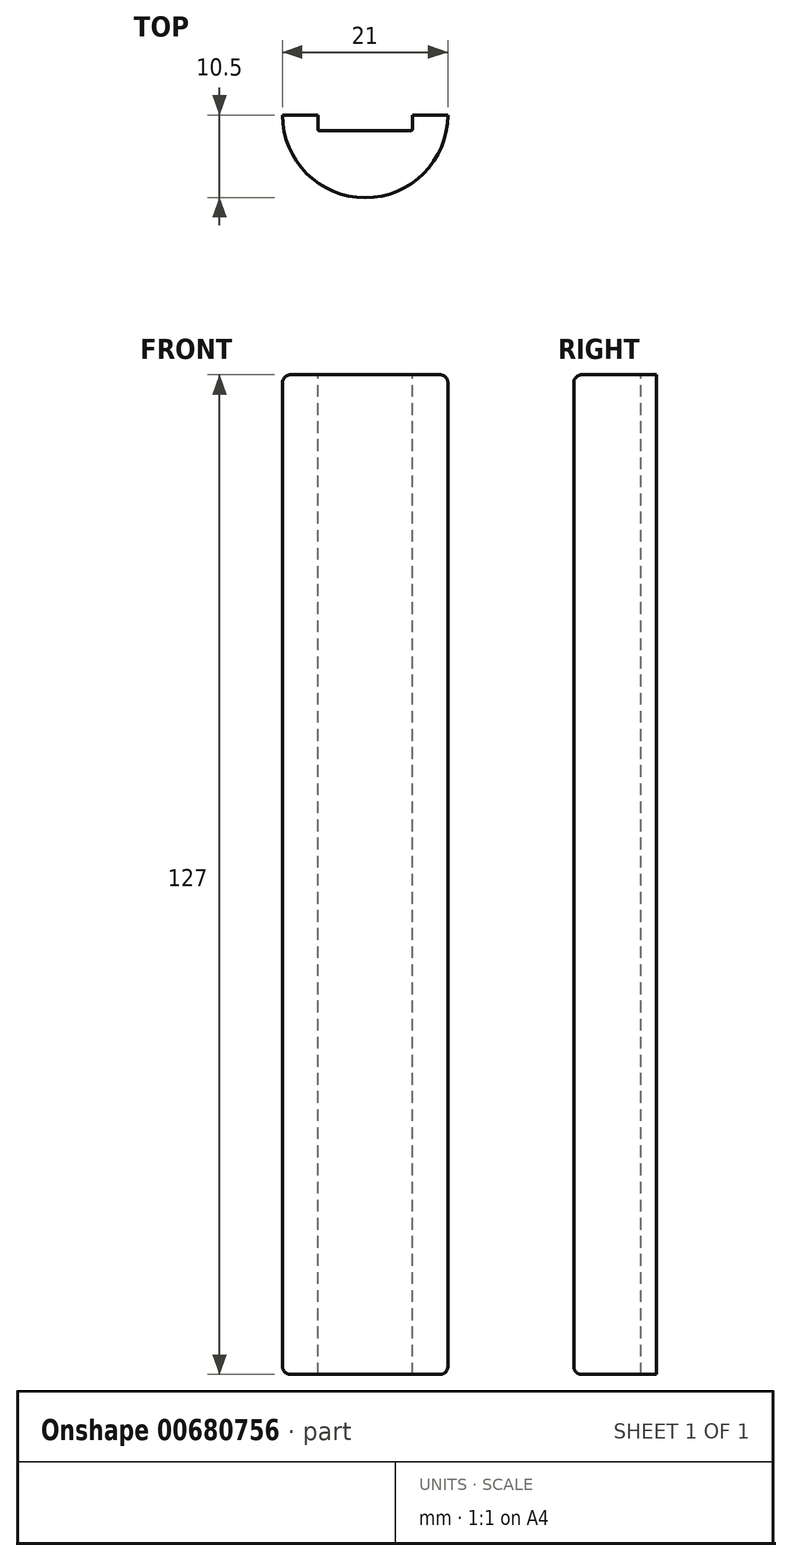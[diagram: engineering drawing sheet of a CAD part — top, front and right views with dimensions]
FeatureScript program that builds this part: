
annotation { "Feature Type Name" : "Feature", "Feature Type Description" : "" }
export const myFeature = defineFeature(function(context is Context, id is Id, definition is map)
    precondition{}
    {
        {
            var Q0;
            Q0=qCreatedBy(makeId("Front.planeOp"),FACE);
            var sketch = newSketch(context, id + "F0", { "sketchPlane" : qUnion([Q0])});
            skLineSegment(sketch, "E0.bottom", {"start": v(-5.25, 63.5) * mm, "end": v(5.25, 63.5) * mm});
            skLineSegment(sketch, "E0.top", {"start": v(-5.25, -63.5) * mm, "end": v(5.25, -63.5) * mm});
            skLineSegment(sketch, "E0.left", {"start": v(-5.25, 63.5) * mm, "end": v(-5.25, -63.5) * mm});
            skLineSegment(sketch, "E0.right", {"start": v(5.25, 63.5) * mm, "end": v(5.25, -63.5) * mm});
            skPoint(sketch, "E0.middle", {"position": v(0, 0) * mm});
            skSolve(sketch);
        }
        {
            var Q0;
            Q0=makeQuery(id+"F0.imprint","IMPRINT",FACE,{"disambiguationData":[TD([[makeQuery(id+"F0.imprint","IMPRINT",EDGE,{"derivedFrom":sQuery(id+"F0.wireOp",EDGE,"E0.bottom")}),-1.0]])]});
            var Q1;
            Q1=sQuery(id+"F0.wireOp",EDGE,"E0.right");
            revolve(context, id + "F1", {"entities" : qUnion([Q0]), "axis" : qUnion([Q1]), "revolveType" : RevolveType.ONE_DIRECTION, "angle" : 180 * degree});
        }
        {
            var Q0;
            Q0=makeQuery(id+"F1.opRevolve","SWEPT_FACE",FACE,{"disambiguationData":[OSD([sQuery(id+"F0.wireOp",EDGE,"E0.bottom")])]});
            var sketch = newSketch(context, id + "F2", { "sketchPlane" : qUnion([Q0])});
            skLineSegment(sketch, "E1", {"start": v(5.25, 0) * mm, "end": v(11.25, 0) * mm});
            skLineSegment(sketch, "E2", {"start": v(5.25, 0) * mm, "end": v(-0.75, 0) * mm});
            skLineSegment(sketch, "E3", {"start": v(-0.75, 0) * mm, "end": v(-0.75, 1.8) * mm});
            skLineSegment(sketch, "E4", {"start": v(-0.55, 2) * mm, "end": v(11.05, 2) * mm});
            skLineSegment(sketch, "E5", {"start": v(11.25, 1.8) * mm, "end": v(11.25, 0) * mm});
            skPoint(sketch, "E6.visualSharp", {"position": v(-0.75, 2) * mm});
            skArc(sketch, "E6.filletArc", {"start": v(-0.55, 2) * mm, "mid": v(-0.7, 1.94) * mm, "end": v(-0.75, 1.8) * mm});
            skPoint(sketch, "E7.visualSharp", {"position": v(11.25, 2) * mm});
            skArc(sketch, "E7.filletArc", {"start": v(11.25, 1.8) * mm, "mid": v(11.2, 1.94) * mm, "end": v(11.05, 2) * mm});
            skSolve(sketch);
        }
        {
            var Q0;
            Q0=makeQuery(id+"F2.imprint","IMPRINT",FACE,{"disambiguationData":[TD([[makeQuery(id+"F2.imprint","IMPRINT",EDGE,{"derivedFrom":sQuery(id+"F2.wireOp",EDGE,"E1")}),-1.0]])]});
            extrude(context, id + "F3", {"entities" : qUnion([Q0]), "operationType" : NewBodyOperationType.REMOVE, "oppositeDirection" : true, "depth" : 127 * mm, "offsetDistance" : 25 * mm});
        }
        {
            var Q0;
            Q0=makeQuery(id+"F1.opRevolve","SWEPT_EDGE",EDGE,{"disambiguationData":[OSD([sQuery(id+"F0.wireOp",EDGE,"E0.bottom"),sQuery(id+"F0.wireOp",EDGE,"E0.left")])]});
            fillet(context, id + "F4", {"entities" : qUnion([Q0]), "radius" : 1 * mm, "tangentPropagation" : true, "allowEdgeOverflow" : false});
        }
        {
            var Q0;
            Q0=makeQuery(id+"F1.opRevolve","SWEPT_EDGE",EDGE,{"disambiguationData":[OSD([sQuery(id+"F0.wireOp",EDGE,"E0.top"),sQuery(id+"F0.wireOp",EDGE,"E0.left")])]});
            fillet(context, id + "F5", {"entities" : qUnion([Q0]), "radius" : 1 * mm, "tangentPropagation" : true, "allowEdgeOverflow" : false});
        }
        {
            var Q0;
            Q0=makeQuery(id+"F1.opRevolve","SWEPT_BODY",BODY,{"disambiguationData":[OSD([sQuery(id+"F0.wireOp",EDGE,"E0.bottom"),sQuery(id+"F0.wireOp",EDGE,"E0.top"),sQuery(id+"F0.wireOp",EDGE,"E0.left"),sQuery(id+"F0.wireOp",EDGE,"E0.right")])]});
            var Q1;
            Q1=qCreatedBy(makeId("Front.planeOp"),FACE);
            mirror(context, id + "F6", {"entities" : qUnion([Q0]), "mirrorPlane" : qUnion([Q1])});
        }
        {
            var Q0;
            Q0=makeQuery(id+"F1.opRevolve","SWEPT_BODY",BODY,{"disambiguationData":[OSD([sQuery(id+"F0.wireOp",EDGE,"E0.bottom"),sQuery(id+"F0.wireOp",EDGE,"E0.top"),sQuery(id+"F0.wireOp",EDGE,"E0.left"),sQuery(id+"F0.wireOp",EDGE,"E0.right")])]});
            deleteBodies(context, id + "F7", {"entities" : qUnion([Q0])});
        }
    });
